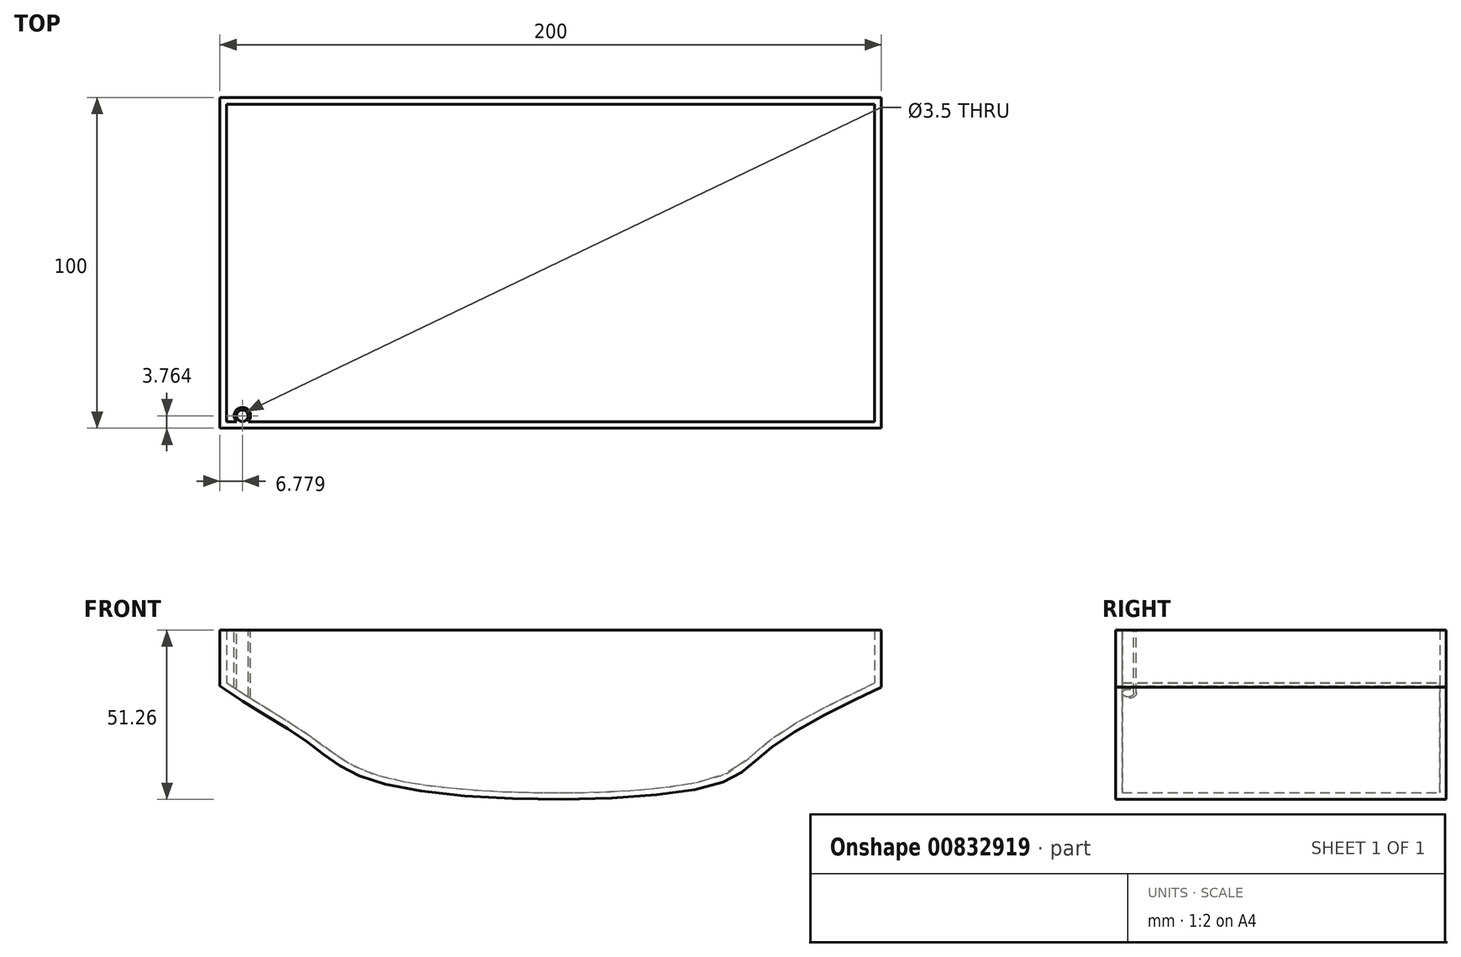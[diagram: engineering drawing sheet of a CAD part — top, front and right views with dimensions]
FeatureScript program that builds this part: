
annotation { "Feature Type Name" : "Feature", "Feature Type Description" : "" }
export const myFeature = defineFeature(function(context is Context, id is Id, definition is map)
    precondition{}
    {
        {
            var Q0;
            Q0=qCreatedBy(makeId("Front.planeOp"),FACE);
            var sketch = newSketch(context, id + "F0", { "sketchPlane" : qUnion([Q0])});
            skLineSegment(sketch, "E0.bottom", {"start": v(-100, 20) * mm, "end": v(100, 20) * mm});
            skLineSegment(sketch, "E0.left", {"start": v(-100, 20) * mm, "end": v(-100, 3.02) * mm});
            skLineSegment(sketch, "E0.right", {"start": v(100, 20) * mm, "end": v(100, 2.72) * mm});
            skFitSpline(sketch, "E1", {"points": [v(-104.22, 6.16) * mm, v(-73.59, -13.88) * mm, v(-50, -26.72) * mm, v(50, -26.72) * mm, v(69.88, -13.2) * mm, v(104.79, 5.26) * mm, v(104.11, 5.26) * mm], "startDerivative": vector(155.69, -123.2) * mm, "endDerivative": vector(-42.05, -6.81) * mm});
            skPoint(sketch, "E2.orphan", {"position": v(0, -14.44) * mm});
            skPoint(sketch, "E3.end.orphan", {"position": v(0, -64.44) * mm});
            skSolve(sketch);
        }
        {
            var Q0;
            Q0=makeQuery(id+"F0.imprint","IMPRINT",FACE,{"disambiguationData":[TD([[makeQuery(id+"F0.imprint","IMPRINT",EDGE,{"derivedFrom":sQuery(id+"F0.wireOp",EDGE,"E0.bottom")}),-1.0]])]});
            extrude(context, id + "F1", {"entities" : qUnion([Q0]), "depth" : 100 * mm, "offsetDistance" : 25 * mm});
        }
        {
            var Q0;
            Q0=makeQuery(id+"F1.opExtrude","SWEPT_FACE",FACE,{"disambiguationData":[OSD([sQuery(id+"F0.wireOp",EDGE,"E0.bottom")])]});
            shell(context, id + "F2", {"entities" : qUnion([Q0]), "thickness" : 2 * mm});
        }
        {
            var Q0;
            Q0=makeQuery(id+"F1.opExtrude","SWEPT_FACE",FACE,{"disambiguationData":[OSD([sQuery(id+"F0.wireOp",EDGE,"E0.bottom")])]});
            var sketch = newSketch(context, id + "F3", { "sketchPlane" : qUnion([Q0])});
            skCircle(sketch, "E4", {"center": v(-93.22, -96.24) * mm, "radius": 1.75 * mm});
            skCircle(sketch, "E5", {"center": v(-93.22, -96.24) * mm, "radius": 2.5 * mm});
            skLineSegment(sketch, "E6", {"start": v(0, 25.4) * mm, "end": v(0, -103.38) * mm});
            skSolve(sketch);
        }
        {
            var Q0;
            Q0=makeQuery(id+"F3.imprint","IMPRINT",FACE,{"disambiguationData":[TD([[makeQuery(id+"F3.imprint","IMPRINT",EDGE,{"derivedFrom":sQuery(id+"F3.wireOp",EDGE,"E4")}),-1.0]])]});
            extrude(context, id + "F4", {"entities" : qUnion([Q0]), "operationType" : NewBodyOperationType.ADD, "endBound" : BoundingType.UP_TO_NEXT, "oppositeDirection" : true, "depth" : 25 * mm, "offsetDistance" : 25 * mm});
        }
    });
